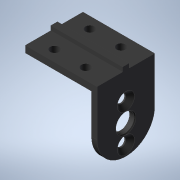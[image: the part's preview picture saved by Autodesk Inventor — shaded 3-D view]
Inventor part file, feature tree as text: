
AUTODESK INVENTOR PART (.ipt)
format: ipt  version: 2021 (Build 250183000, 183)  size: 377,856 bytes
history: native  units: mm
features: extrude x4, other x3, chamfer x2, sketch x2, fillet x1
ambient origin geometry x8: Origin, YZ Plane, XZ Plane, XY Plane, X Axis, Y Axis, Z Axis, Center Point
bodies: Body1 (feature_tree)
feature tree (12):
  other  "00_Mastersketch.ipt"
  extrude  "Extrusion2"  Depth=26.3mm
  extrude  "Extrusion3"  TaperAngle=0.0deg  [1 undecoded]
  extrude  "Extrusion4"  Depth=3.0mm
  fillet  "Rundung2"  Radius=3.9mm
  chamfer  "Fase2"  [1 undecoded]
  chamfer  "Fase3"  Distance=2.0mm Angle=45.0deg
  extrude  "Extrusion5"  Depth=2.0mm TaperAngle=45.0deg
  other  "01_caseBottom"
  other  "06_motorHolderSketch"
  sketch  "Skizze6"  dims[d0=10.0mm d36=26.3mm]
  sketch  "Skizze7"  dims[d37=0.0mm d38=0.0mm d39=0.0mm d40=8.4mm d41=3.9mm d42=0.0mm d43=0.0mm d44=2.0mm d45=2.0mm d46=45.0deg d47=0.4mm d48=2.0mm d49=45.0deg d50=0.3mm d51=2.0mm d52=3.0mm d53=0.0mm]
note: 2 required parameter values undecoded (feature->parameter linkage not recoverable at this tier; creation-order binding heuristic only, values carry confidence <= 0.55)
